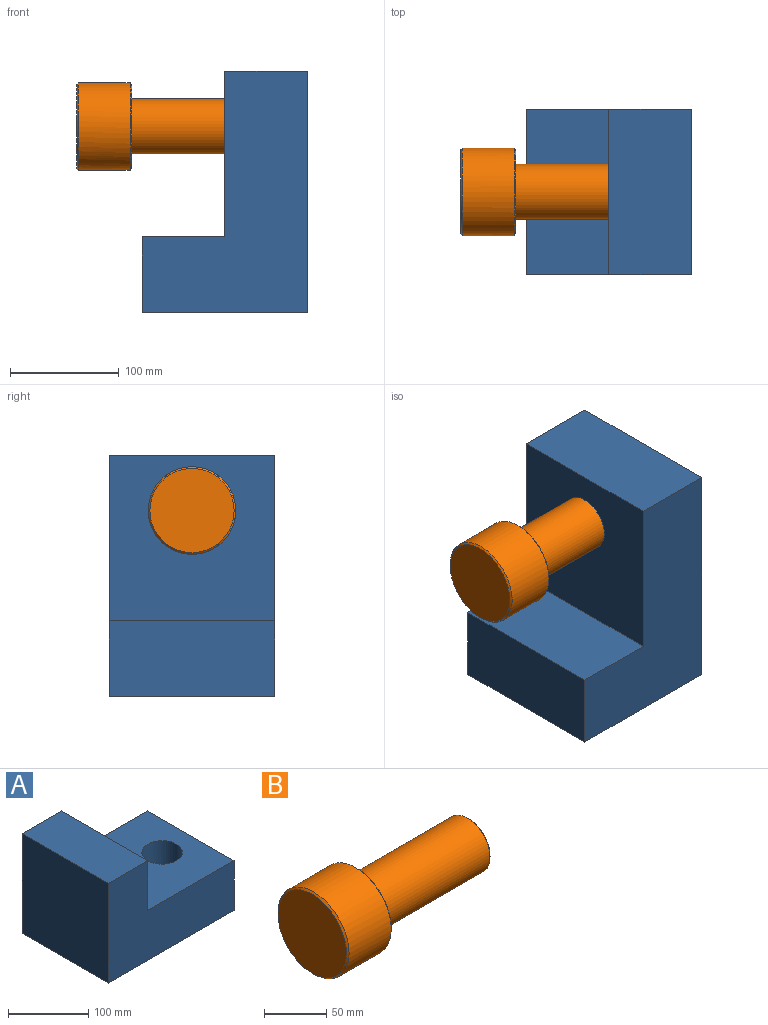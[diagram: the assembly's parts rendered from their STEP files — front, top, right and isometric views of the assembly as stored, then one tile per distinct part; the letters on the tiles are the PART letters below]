
ASSEMBLY  parts=2 mates=1
PART A: 9 faces, bbox 222.3x152.4x152.4 mm
  f0: plane 222.25x152.4mm, normal (0,0,-1), area 31844.1mm2, adj f1,f5,f6,f7,f8
  f1: plane 152.4x76.2mm, normal (1,0,0), area 11612.9mm2, adj f0,f2,f6,f7
  f2: plane 152.4x152.4mm, normal (0,0,1), area 21198.9mm2, adj f1,f3,f6,f7,f8
  f3: plane 152.4x76.2mm, normal (1,0,0), area 11612.9mm2, adj f2,f4,f6,f7
  f4: plane 152.4x69.85mm, normal (0,0,1), area 10645.1mm2, adj f3,f5,f6,f7
  f5: plane 152.4x152.4mm, normal (-1,0,0), area 23225.8mm2, adj f0,f4,f6,f7
  f6: plane 222.25x152.4mm, normal (0,-1,0), area 22258mm2, adj f0,f1,f2,f3,f4,f5
  f7: plane 222.25x152.4mm, normal (0,1,0), area 22258mm2, adj f0,f1,f2,f3,f4,f5
  f8: cylinder r=25.4mm len=76.2mm, axis (0,0,1), area 12161mm2, adj f0,f2
PART B: 8 faces, bbox 177.8x80.6x80.6 mm
  f0: plane 47.7x47.7mm, normal (1,0,0), area 1787.1mm2, adj f5
  f1: cylinder r=25.37mm len=125.48mm, axis (-1,0,0), area 20005.1mm2, adj f2,f5
  f2: plane 77.58x77.58mm, normal (1,0,0), area 2704.7mm2, adj f1,f7
  f3: cylinder r=40.32mm len=80.63mm, axis (-1,0,0), area 12096.2mm2, adj f6,f7
  f4: plane 77.58x77.58mm, normal (-1,0,0), area 4727.5mm2, adj f6
  f5: cone r=25.37mm half-angle=45deg, axis (-1,0,0), area 333.3mm2, adj f0,f1
  f6: cone r=38.79mm half-angle=45deg, axis (1,0,0), area 535.6mm2, adj f3,f4
  f7: cone r=40.32mm half-angle=45deg, axis (-1,0,0), area 535.6mm2, adj f2,f3
PLACE A rot(axis=(0,-1,0),90deg) t=(-81.2,15.93,256.49)mm
PLACE B t=(-116.11,15.93,205.69)mm
MATE slider A.f8 <-> B.f1  axis (-1,0,0) through (-157.4,15.93,205.69)mm
